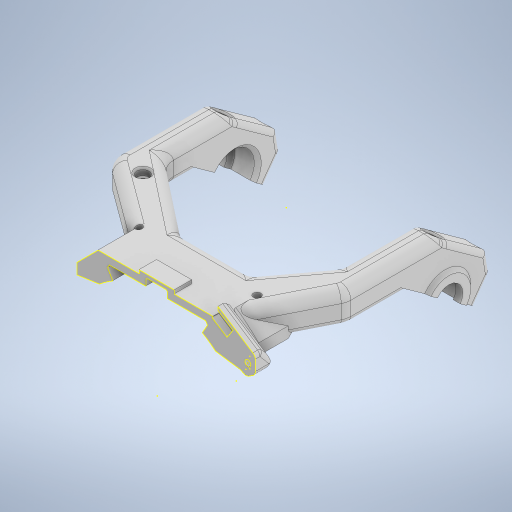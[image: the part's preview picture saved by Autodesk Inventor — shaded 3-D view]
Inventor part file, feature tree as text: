
AUTODESK INVENTOR PART (.ipt)
format: ipt  version: 2023.4 (Build 274418000, 418)  size: 1,242,624 bytes
history: native  units: mm
features: sketch x28, extrude x26, projected_geometry x15, chamfer x13, fillet x6, plane x3, thicken_offset x3, other x3, reference x2
ambient origin geometry x8: Origin, YZ Plane, XZ Plane, XY Plane, X Axis, Y Axis, Z Axis, Center Point
bodies: Solid1 (feature_tree)
feature tree (99):
  extrude  "Extrusion1"  Depth=70.0mm
  extrude  "Extrusion2"  Depth=17.0mm TaperAngle=0.0deg
  extrude  "Extrusion3"  Depth=10.0mm TaperAngle=0.0deg
  extrude  "Extrusion4"  Depth=10.0mm TaperAngle=0.0deg
  extrude  "Extrusion5"  Depth=10.0mm TaperAngle=0.0deg
  extrude  "Extrusion6"  TaperAngle=0.0deg  [1 undecoded]
  sketch  "Sketch9"  dims[d21=0.0mm d22=0.0mm d23=1.0mm d24=0.0mm]
  extrude  "Extrusion7"  Depth=1.0mm TaperAngle=0.0deg
  extrude  "Extrusion8"  Depth=8.0mm
  extrude  "Extrusion9"  Depth=8.0mm
  extrude  "Extrusion10"  Depth=6.0mm TaperAngle=0.0deg
  extrude  "Extrusion11"  Depth=4.0mm TaperAngle=0.0deg
  extrude  "Extrusion12"  Depth=4.0mm TaperAngle=0.0deg
  extrude  "Extrusion13"  Depth=8.0mm TaperAngle=45.0deg
  extrude  "Extrusion14"  Depth=5.0mm TaperAngle=0.0deg
  chamfer  "Chamfer1"  [1 undecoded]
  extrude  "Extrusion15"  Depth=3.0mm
  chamfer  "Chamfer2"  Distance=3.0mm
  chamfer  "Chamfer3"  Distance=2.0mm
  chamfer  "Chamfer5"  Distance=2.0mm
  extrude  "Extrusion17"  Depth=6.0mm
  plane  "Work Plane1"
  extrude  "Extrusion18"  Depth=3.0mm
  thicken_offset  "Thicken1"
  extrude  "Extrusion19"  Depth=3.0mm TaperAngle=45.0deg
  plane  "Work Plane2"
  extrude  "Extrusion20"  Depth=3.0mm
  extrude  "Extrusion21"  Depth=3.0mm
  chamfer  "Chamfer7"  Distance=0.2mm
  fillet  "Fillet4"  Radius=2.0mm
  fillet  "Fillet5"  Radius=3.3mm
  fillet  "Fillet6"  [1 undecoded]
  fillet  "Fillet7"  Radius=7.0mm
  chamfer  "Chamfer8"  Distance=4.0mm
  thicken_offset  "Thicken2"
  thicken_offset  "Thicken3"
  chamfer  "Chamfer9"  Distance=1.0mm Angle=45.0deg
  extrude  "Extrusion22"  [1 undecoded]
  extrude  "Extrusion23"  Depth=3.0mm TaperAngle=0.0deg
  chamfer  "Chamfer10"  Distance=3.0mm
  plane  "Work Plane3"
  extrude  "Extrusion24"  Depth=3.0mm TaperAngle=45.0deg
  extrude  "Extrusion25"  Depth=3.0mm TaperAngle=45.0deg
  chamfer  "Chamfer11"  Distance=1.2mm Angle=45.0deg
  chamfer  "Chamfer12"  Distance=2.0mm Angle=45.0deg
  chamfer  "Chamfer13"  Distance=10.0mm
  chamfer  "Chamfer14"  Distance=9.0mm
  fillet  "Fillet8"  Radius=4.0mm
  extrude  "Extrusion26"  Depth=3.0mm
  extrude  "Extrusion27"  Depth=3.0mm TaperAngle=45.0deg
  chamfer  "Chamfer15"  Distance=3.0mm
  fillet  "Fillet10"  [1 undecoded]
  sketch  "Sketch36"  dims[d100=0.2mm d101=0.2mm d102=0.2mm d103=0.2mm d104=2.0mm d105=2.0mm d106=45.0deg d107=3.3mm d108=0.0mm d109=0.0mm d110=7.0mm d111=4.0mm d112=0.0mm d113=1.0mm d114=2.0mm d115=45.0deg d116=-5.0mm d117=3.0mm d118=0.0mm d119=3.0mm d120=0.0mm d121=3.0mm d122=2.0mm d123=45.0deg d124=1.41mm d125=2.0mm d126=45.0deg d127=1.2mm d128=2.0mm d129=45.0deg d130=2.0mm d131=2.0mm d132=45.0deg d133=10.0mm d134=9.0mm d135=0.0mm d137=4.0mm d138=0.0mm d139=3.4mm d140=5.0mm d141=2.0mm d142=45.0deg d143=3.0mm d144=0.0mm d145=0.0mm d146=0.0mm]
  sketch  "Sketch1"  dims[d0=30.0mm d1=0.0mm d2=70.0mm]
  sketch  "Sketch4"  dims[d3=70.0mm d4=17.0mm d5=0.0mm]
  projected_geometry  "Projected Loop3"
  sketch  "Sketch5"  dims[d6=17.0mm d7=0.0mm d8=10.0mm d9=0.0mm]
  projected_geometry  "Projected Loop4"
  sketch  "Sketch6"  dims[d10=4.2mm d11=10.0mm d12=0.0mm]
  projected_geometry  "Projected Loop5"
  projected_geometry  "Projected Loop6"
  sketch  "Sketch7"  dims[d13=0.0mm d14=0.0mm d15=10.0mm d16=0.0mm]
  sketch  "Sketch8"  dims[d17=10.0mm d18=0.0mm d19=0.0mm d20=0.0mm]
  sketch  "Sketch10"  dims[d25=0.5mm d26=0.0mm d27=8.0mm]
  projected_geometry  "Projected Loop7"
  sketch  "Sketch11"  dims[d28=8.0mm d29=8.0mm]
  projected_geometry  "Projected Loop8"
  projected_geometry  "Projected Loop9"
  sketch  "Sketch12"  dims[d30=8.0mm d31=6.0mm d32=0.0mm]
  sketch  "Sketch13"  dims[d33=16.0mm d34=4.0mm d35=0.0mm]
  sketch  "Sketch15"  dims[d36=2.0mm d37=2.0mm d38=45.0deg d39=4.0mm d40=0.0mm]
  sketch  "Sketch16"  dims[d41=2.0mm d42=2.0mm d43=45.0deg d46=8.0mm d47=2.0mm d48=45.0deg]
  projected_geometry  "Projected Loop10"
  projected_geometry  "Projected Loop11"
  sketch  "Sketch17"  dims[d53=1.0mm d54=2.0mm d55=45.0deg d66=5.0mm d67=0.0mm]
  sketch  "Sketch18"  dims[d68=4.3mm]
  sketch  "Sketch19"  dims[d69=4.3mm]
  projected_geometry  "Projected Loop12"
  projected_geometry  "Projected Loop13"
  sketch  "Sketch23"  dims[d70=20.0mm]
  sketch  "Sketch25"  dims[d71=20.0mm]
  sketch  "Sketch26"  dims[d72=12.0mm]
  projected_geometry  "Projected Loop14"
  sketch  "Sketch27"  dims[d73=12.0mm d74=0.0mm d75=0.0mm]
  sketch  "Sketch28"  dims[d76=0.1mm d77=0.1mm d78=3.0mm d79=0.0mm]
  projected_geometry  "Projected Loop15"
  sketch  "Sketch29"  dims[d80=20.0mm]
  sketch  "Sketch30"  dims[d81=10.0mm]
  sketch  "Sketch32"  dims[d82=4.0mm d83=2.0mm d84=0.0mm d88=2.0mm d89=0.0mm]
  sketch  "Sketch33"  dims[d90=12.0mm d91=2.0mm d92=45.0deg d93=6.0mm]
  projected_geometry  "Projected Loop16"
  sketch  "Sketch34"  dims[d94=3.0mm d95=3.0mm]
  reference  "Reference26"
  sketch  "Sketch35"  dims[d96=3.0mm d97=1.0mm d98=2.0mm d99=45.0deg]
  reference  "Reference27"
  projected_geometry  "Projected Loop17"
  parser-record x1  (decoder bookkeeping rows leaked as tree rows — omitted from the tree; the rows remain in map.json)
  other  "MK3_Assembly.iam"
  other  "separator_top_mid:1"
note: 5 required parameter values undecoded (feature->parameter linkage not recoverable at this tier; creation-order binding heuristic only, values carry confidence <= 0.55)
note: 1 file-system path scrubbed to <path> (originals preserved in map.json)
